# Revit family: Deca_Chuveiro Redondo de Parede_Flex Max_2085.STD
name_source: partatom
category: Plumbing Fixtures
units: mm (PartAtom-declared; Revit-internal decimal feet)

## family parameters
Cut with Voids When Loaded = No
Host = Face
Part Type = Normal
Room Calculation Point = No
Round Connector Dimension = Use Radius
Shared = No

## types (3) — shared parameters
Acompanha o Produto = RESTRITOR DE VAZÃO
Aprovado por = quattroD
Atendimento ao Cliente = 0800 011 7073
Categoria = CHUVEIROS E DUCHAS
Composição Anel Vedação = -
Composição Assento = -
Composição Básica = Liga de Cobre (bronze e latão),Plásticos de Engenharia,Elastômeros
Composição Componente = -
Consumo = -
Cor Interna = -
Cor Secundária = Preto
Cores Componente = -
Criado por = quattroD
Código Pai = 2085.C.STD
Default Elevation = 2.2 m
Diâmetro Água Fria = 0.02 m
Informações Complementares = -
Itens de Instalação = -
Linha = Flex
Manufacturer = Deca
Material secundário = Deca_Preto
Norma = NBR 15206
Peso Líquido (Kg) = 1.05
Pressão mín. Aquec. Acúmulo = 4 MCA
Pressão mín. Aquec. Passagem = 8 MCA
Raio Água Fria = 0.01 m
Saída de Esgoto = -
Segmento = -
Tipo de dispositivo economizador = RESTRITOR VAZÃO DE 12L/MIN
Tipo de mecanismo utilizado = -
Tipo de rosca de entrada = BSP NBR 8133
Tipo de rosca de saída = -
URL = www.deca.com.br
Vazão na Pressão máx. (L/min) = 30
Vazão na Pressão mín. (L/min) = 6
zero-valued in all types: HWFU

## per-type parameters (varying)
| type | Cor Principal | Description | Material | Model |
| 2085.C.STD_Cromado | Cromado | CHUVEIRO REDONDO PAREDE CR (220mm) | Deca_Cromado | 2085.C.STD |
| 2085.BL.STD.MT_Black Matte | Black Matte | CHUVEIRO REDONDO PAREDE BL MT (220mm) | Deca_Black Matte | 2085.BL.STD.MT |
| 2085.SM.STD.MT_Summer Gold | Summer Gold | CHUVEIRO REDONDO PAREDE SM MT (220mm) | Deca_Summer Gold | 2085.SM.STD.MT |

note: source unit labels omitted for Vazão na Pressão máx. (L/min), Vazão na Pressão mín. (L/min) — the stored unit's dimension contradicts the parameter name (converter mislabeling)

## geometry (parser evidence)
native form markers: Sweep x3
no freeform markers — native parametric forms only
